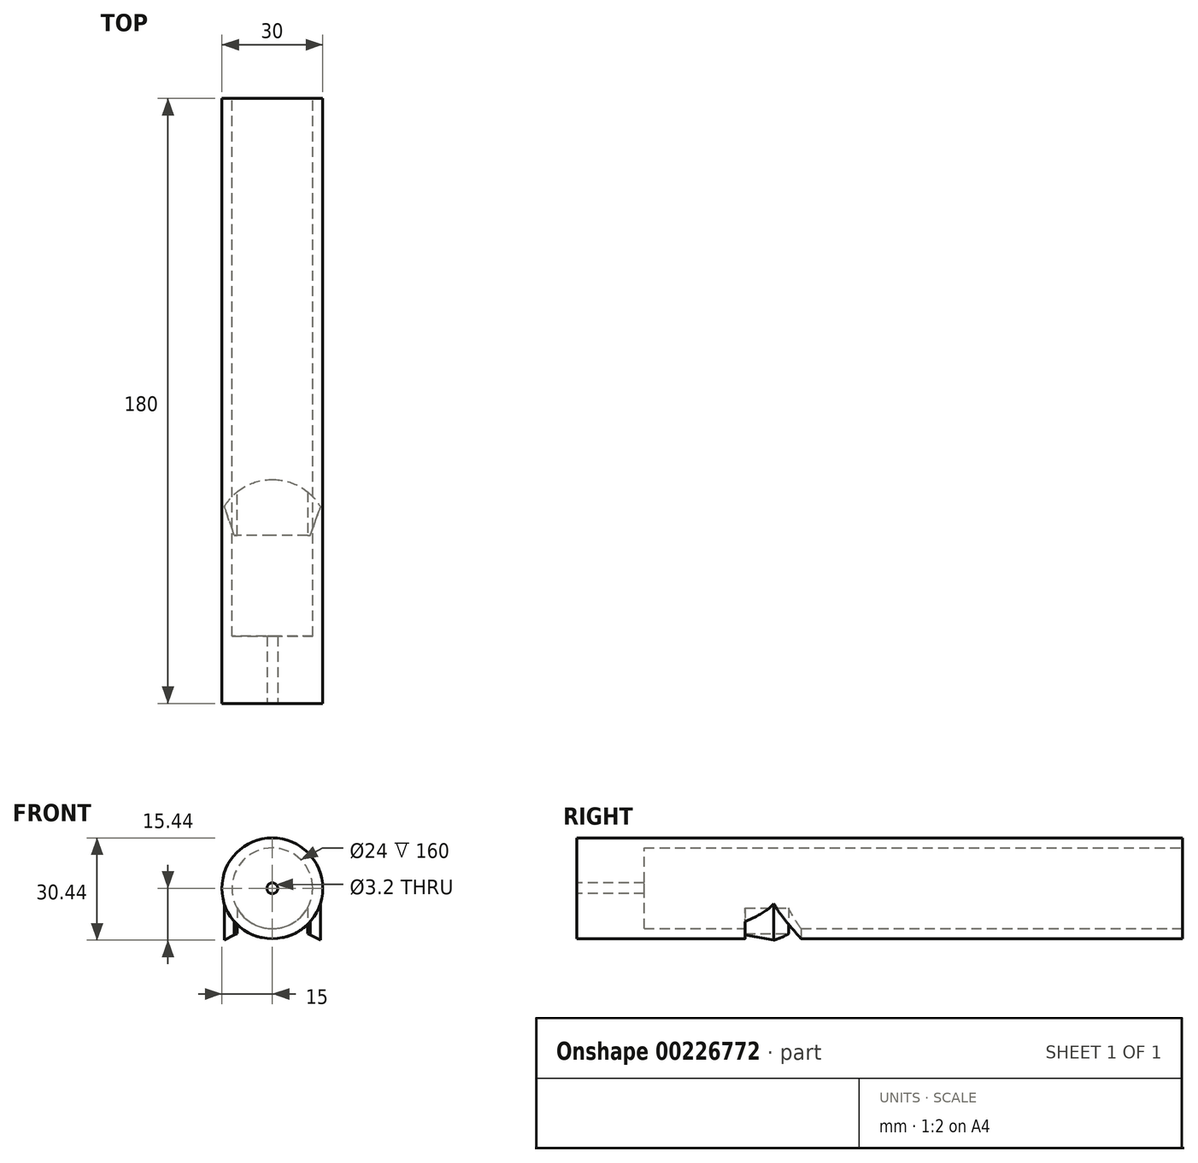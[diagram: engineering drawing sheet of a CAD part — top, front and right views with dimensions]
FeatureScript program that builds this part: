
annotation { "Feature Type Name" : "Feature", "Feature Type Description" : "" }
export const myFeature = defineFeature(function(context is Context, id is Id, definition is map)
    precondition{}
    {
        {
            var Q0;
            Q0=qCreatedBy(makeId("Front.planeOp"),FACE);
            var sketch = newSketch(context, id + "F0", { "sketchPlane" : qUnion([Q0])});
            skCircle(sketch, "E0", {"center": v(0, 0) * mm, "radius": 15 * mm});
            skCircle(sketch, "E1", {"center": v(0, 0) * mm, "radius": 12 * mm});
            skSolve(sketch);
        }
        {
            var Q0;
            Q0=makeQuery(id+"F0.imprint","IMPRINT",FACE,{"disambiguationData":[TD([[makeQuery(id+"F0.imprint","IMPRINT",EDGE,{"derivedFrom":sQuery(id+"F0.wireOp",EDGE,"E0")}),1.0]])]});
            var Q1;
            Q1=makeQuery(id+"F0.imprint","IMPRINT",FACE,{"disambiguationData":[TD([[makeQuery(id+"F0.imprint","IMPRINT",EDGE,{"derivedFrom":sQuery(id+"F0.wireOp",EDGE,"E1")}),1.0]])]});
            extrude(context, id + "F1", {"entities" : qUnion([Q0, Q1]), "depth" : 180 * mm});
        }
        {
            var Q0;
            Q0=makeQuery(id+"F0.imprint","IMPRINT",FACE,{"disambiguationData":[TD([[makeQuery(id+"F0.imprint","IMPRINT",EDGE,{"derivedFrom":sQuery(id+"F0.wireOp",EDGE,"E1")}),1.0]])]});
            extrude(context, id + "F2", {"entities" : qUnion([Q0]), "operationType" : NewBodyOperationType.REMOVE, "depth" : 160 * mm});
        }
        {
            var Q0;
            Q0=qCreatedBy(makeId("Top.planeOp"),FACE);
            cPlane(context, id + "F3", {"entities" : qUnion([Q0]), "cplaneType" : CPlaneType.OFFSET, "offset" : 15 * mm, "oppositeDirection" : true, "width" : 150 * mm, "height" : 150 * mm});
        }
        {
            var Q0;
            Q0=qCreatedBy(id+"F3.planeOp",FACE);
            var sketch = newSketch(context, id + "F4", { "sketchPlane" : qUnion([Q0])});
            skLineSegment(sketch, "E2.bottom", {"start": v(0, -97.19) * mm, "end": v(7, -97.19) * mm});
            skLineSegment(sketch, "E2.top", {"start": v(0, -130) * mm, "end": v(7, -130) * mm});
            skLineSegment(sketch, "E2.left", {"start": v(0, -97.19) * mm, "end": v(0, -130) * mm});
            skLineSegment(sketch, "E2.right", {"start": v(7, -97.19) * mm, "end": v(7, -112.8) * mm});
            skLineSegment(sketch, "E3", {"start": v(0, 0) * mm, "end": v(0, -235.04) * mm, "construction": true});
            skLineSegment(sketch, "E4.bottom", {"start": v(0, -130) * mm, "end": v(-7, -130) * mm});
            skLineSegment(sketch, "E4.top", {"start": v(0, -97.19) * mm, "end": v(-7, -97.19) * mm});
            skLineSegment(sketch, "E4.left", {"start": v(0, -130) * mm, "end": v(0, -97.19) * mm});
            skLineSegment(sketch, "E4.right", {"start": v(-7, -112.8) * mm, "end": v(-7, -97.19) * mm});
            skCircle(sketch, "E5", {"center": v(0, -130) * mm, "radius": 18.58 * mm});
            skCircle(sketch, "E6", {"center": v(0, -130) * mm, "radius": 16.65 * mm});
            skLineSegment(sketch, "E7", {"start": v(18.58, -130) * mm, "end": v(-18.58, -130) * mm});
            skLineSegment(sketch, "E8", {"start": v(10.5, -130) * mm, "end": v(10.5, -117.08) * mm});
            skPoint(sketch, "E9.start.orphan", {"position": v(-9, -130) * mm});
            skLineSegment(sketch, "E10.MirrorCS", {"start": v(-10.5, -130) * mm, "end": v(-10.5, -117.08) * mm});
            skLineSegment(sketch, "E11", {"start": v(11.3, -130) * mm, "end": v(14.29, -121.45) * mm});
            skLineSegment(sketch, "E12.MirrorCS", {"start": v(-11.3, -130) * mm, "end": v(-14.29, -121.45) * mm});
            skSolve(sketch);
        }
        {
            var Q0;
            {var subQ1=sQuery(id+"F4.wireOp",EDGE,"E2.top");Q0=makeQuery(id+"F4.imprint","IMPRINT",FACE,{"disambiguationData":[TD([[makeQuery(id+"F4.imprint","IMPRINT",EDGE,{"derivedFrom":subQ1}),1.0]])]});}
            var Q1;
            {var subQ1=sQuery(id+"F4.wireOp",EDGE,"E4.bottom");Q1=makeQuery(id+"F4.imprint","IMPRINT",FACE,{"disambiguationData":[TD([[makeQuery(id+"F4.imprint","IMPRINT",EDGE,{"derivedFrom":subQ1}),-1.0]])]});}
            extrude(context, id + "F5", {"entities" : qUnion([Q0, Q1]), "operationType" : NewBodyOperationType.REMOVE, "depth" : 20 * mm});
        }
        {
            var Q0;
            {var subQ0=sQuery(id+"F4.wireOp",EDGE,"E8");Q0=makeQuery(id+"F4.imprint","IMPRINT",FACE,{"disambiguationData":[TD([[makeQuery(id+"F4.imprint","IMPRINT",EDGE,{"derivedFrom":subQ0}),-1.0]])]});}
            var Q1;
            {var subQ0=sQuery(id+"F4.wireOp",EDGE,"E10.MirrorCS");Q1=makeQuery(id+"F4.imprint","IMPRINT",FACE,{"disambiguationData":[TD([[makeQuery(id+"F4.imprint","IMPRINT",EDGE,{"derivedFrom":subQ0}),1.0]])]});}
            extrude(context, id + "F6", {"entities" : qUnion([Q0, Q1]), "operationType" : NewBodyOperationType.ADD, "depth" : 18 * mm});
        }
        {
            var Q0;
            {var subQ0=sQuery(id+"F4.wireOp",EDGE,"E10.MirrorCS");Q0=makeQuery(id+"F4.imprint","IMPRINT",FACE,{"disambiguationData":[TD([[makeQuery(id+"F4.imprint","IMPRINT",EDGE,{"derivedFrom":subQ0}),1.0]])]});}
            var Q1;
            {var subQ0=sQuery(id+"F4.wireOp",EDGE,"E8");Q1=makeQuery(id+"F4.imprint","IMPRINT",FACE,{"disambiguationData":[TD([[makeQuery(id+"F4.imprint","IMPRINT",EDGE,{"derivedFrom":subQ0}),-1.0]])]});}
            extrude(context, id + "F7", {"entities" : qUnion([Q0, Q1]), "operationType" : NewBodyOperationType.ADD, "oppositeDirection" : true, "depth" : .5 * mm});
        }
        {
            var Q0;
            Q0=makeQuery(id+"F0.imprint","IMPRINT",FACE,{"disambiguationData":[TD([[makeQuery(id+"F0.imprint","IMPRINT",EDGE,{"derivedFrom":sQuery(id+"F0.wireOp",EDGE,"E1")}),1.0]])]});
            extrude(context, id + "F8", {"entities" : qUnion([Q0]), "operationType" : NewBodyOperationType.REMOVE, "depth" : 160 * mm});
        }
        {
            var Q0;
            Q0=makeQuery(id+"F7.opExtrude","CAP_EDGE",EDGE,{"disambiguationData":[OSD([sQuery(id+"F4.wireOp",EDGE,"E8")])],"isStart":false});
            chamfer(context, id + "F9", {"entities" : qUnion([Q0]), "chamferType" : ChamferType.TWO_OFFSETS, "width1" : 3.9 * mm, "oppositeDirection" : false, "width2" : 2 * mm, "tangentPropagation" : true});
        }
        {
            var Q0;
            Q0=makeQuery(id+"F7.opExtrude","CAP_EDGE",EDGE,{"disambiguationData":[OSD([sQuery(id+"F4.wireOp",EDGE,"E10.MirrorCS")])],"isStart":false});
            chamfer(context, id + "F10", {"entities" : qUnion([Q0]), "chamferType" : ChamferType.TWO_OFFSETS, "width1" : 2 * mm, "oppositeDirection" : false, "width2" : 3.9 * mm, "tangentPropagation" : true});
        }
        {
            var Q0;
            Q0=makeQuery(id+"F1.opExtrude","CAP_FACE",FACE,{"disambiguationData":[OSD([sQuery(id+"F0.wireOp",EDGE,"E0")])],"isStart":false});
            var sketch = newSketch(context, id + "F11", { "sketchPlane" : qUnion([Q0])});
            skCircle(sketch, "E13", {"center": v(0, 0) * mm, "radius": 1.6 * mm});
            skSolve(sketch);
        }
        {
            var Q0;
            Q0 = qSketchRegion(id + "F11", true);
            var Q1;
            Q1=makeQuery(id+"F11.imprint","IMPRINT",FACE,{"disambiguationData":[TD([[makeQuery(id+"F11.imprint","IMPRINT",EDGE,{"derivedFrom":sQuery(id+"F11.wireOp",EDGE,"E13")}),1.0]])]});
            extrude(context, id + "F12", {"entities" : qUnion([Q0, Q1]), "operationType" : NewBodyOperationType.REMOVE, "oppositeDirection" : true, "depth" : 20 * mm});
        }
    });
